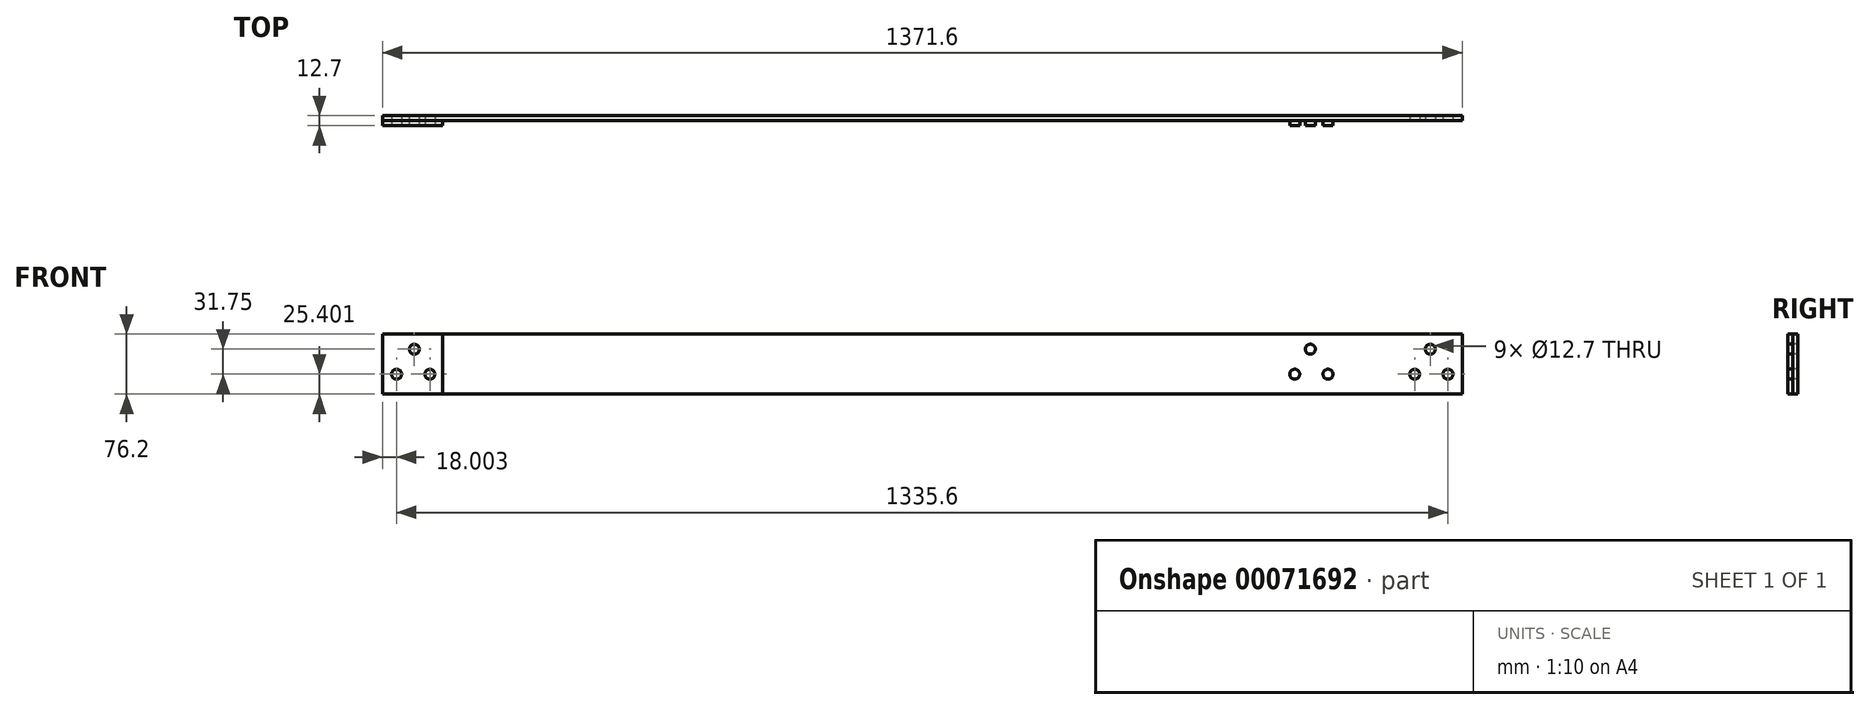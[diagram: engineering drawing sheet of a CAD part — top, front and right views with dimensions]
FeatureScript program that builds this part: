
annotation { "Feature Type Name" : "Feature", "Feature Type Description" : "" }
export const myFeature = defineFeature(function(context is Context, id is Id, definition is map)
    precondition{}
    {
        {
            var Q0;
            Q0=qCreatedBy(makeId("Front.planeOp"),FACE);
            var sketch = newSketch(context, id + "F0", { "sketchPlane" : qUnion([Q0])});
            skLineSegment(sketch, "E0.bottom", {"start": v(-278.67, 72.85) * mm, "end": v(940.53, 72.85) * mm});
            skLineSegment(sketch, "E0.top", {"start": v(-278.67, -3.35) * mm, "end": v(940.53, -3.35) * mm});
            skLineSegment(sketch, "E0.left", {"start": v(-278.67, 72.85) * mm, "end": v(-278.67, -3.35) * mm});
            skLineSegment(sketch, "E0.right", {"start": v(940.53, 72.85) * mm, "end": v(940.53, -3.35) * mm});
            skSolve(sketch);
        }
        {
            var Q0;
            Q0=makeQuery(id+"F0.imprint","IMPRINT",FACE,{"disambiguationData":[TD([[makeQuery(id+"F0.imprint","IMPRINT",EDGE,{"derivedFrom":sQuery(id+"F0.wireOp",EDGE,"E0.bottom")}),-1.0]])]});
            extrude(context, id + "F1", {"entities" : qUnion([Q0]), "depth" : 6.35 * mm});
        }
        {
            var Q0;
            Q0=makeQuery(id+"F1.opExtrude","CAP_FACE",FACE,{"disambiguationData":[OSD([sQuery(id+"F0.wireOp",EDGE,"E0.bottom"),sQuery(id+"F0.wireOp",EDGE,"E0.top"),sQuery(id+"F0.wireOp",EDGE,"E0.left"),sQuery(id+"F0.wireOp",EDGE,"E0.right")])],"isStart":false});
            var sketch = newSketch(context, id + "F2", { "sketchPlane" : qUnion([Q0])});
            skLineSegment(sketch, "E1.0", {"start": v(-278.67, 72.85) * mm, "end": v(940.53, 72.85) * mm});
            skLineSegment(sketch, "E1.1", {"start": v(-278.67, -3.35) * mm, "end": v(940.53, -3.35) * mm});
            skLineSegment(sketch, "E1.2", {"start": v(940.53, 72.85) * mm, "end": v(940.53, -3.35) * mm});
            skLineSegment(sketch, "E1.3", {"start": v(-278.67, 72.85) * mm, "end": v(-278.67, -3.35) * mm});
            skLineSegment(sketch, "E2", {"start": v(-202.47, 72.85) * mm, "end": v(-202.47, -3.35) * mm});
            skCircle(sketch, "E3", {"center": v(-238.17, 53.8) * mm, "radius": 6.35 * mm});
            skCircle(sketch, "E4", {"center": v(-260.67, 22.05) * mm, "radius": 6.35 * mm});
            skCircle(sketch, "E5", {"center": v(-218.33, 22.05) * mm, "radius": 6.35 * mm});
            skLineSegment(sketch, "E6", {"start": v(-278.67, -3.35) * mm, "end": v(-238.17, 53.8) * mm, "construction": true});
            skLineSegment(sketch, "E7", {"start": v(-238.17, 53.8) * mm, "end": v(-202.47, -3.35) * mm, "construction": true});
            skLineSegment(sketch, "E8", {"start": v(330.93, 72.85) * mm, "end": v(330.93, -3.35) * mm, "construction": true});
            skCircle(sketch, "E9.MirrorC", {"center": v(880.2, 22.05) * mm, "radius": 6.35 * mm});
            skCircle(sketch, "E10.MirrorC", {"center": v(900.04, 53.8) * mm, "radius": 6.35 * mm});
            skCircle(sketch, "E11.MirrorC", {"center": v(922.53, 22.05) * mm, "radius": 6.35 * mm});
            skSolve(sketch);
        }
        {
            var Q0;
            Q0=makeQuery(id+"F2.imprint","IMPRINT",FACE,{"disambiguationData":[TD([[makeQuery(id+"F2.imprint","IMPRINT",EDGE,{"derivedFrom":sQuery(id+"F2.wireOp",EDGE,"E3")}),1.0]])]});
            var Q1;
            Q1=makeQuery(id+"F2.imprint","IMPRINT",FACE,{"disambiguationData":[TD([[makeQuery(id+"F2.imprint","IMPRINT",EDGE,{"derivedFrom":sQuery(id+"F2.wireOp",EDGE,"E4")}),1.0]])]});
            var Q2;
            Q2=makeQuery(id+"F2.imprint","IMPRINT",FACE,{"disambiguationData":[TD([[makeQuery(id+"F2.imprint","IMPRINT",EDGE,{"derivedFrom":sQuery(id+"F2.wireOp",EDGE,"E5")}),1.0]])]});
            var Q3;
            Q3=makeQuery(id+"F2.imprint","IMPRINT",FACE,{"disambiguationData":[TD([[makeQuery(id+"F2.imprint","IMPRINT",EDGE,{"derivedFrom":sQuery(id+"F2.wireOp",EDGE,"E10.MirrorC")}),-1.0]])]});
            var Q4;
            Q4=makeQuery(id+"F2.imprint","IMPRINT",FACE,{"disambiguationData":[TD([[makeQuery(id+"F2.imprint","IMPRINT",EDGE,{"derivedFrom":sQuery(id+"F2.wireOp",EDGE,"E9.MirrorC")}),-1.0]])]});
            var Q5;
            Q5=makeQuery(id+"F2.imprint","IMPRINT",FACE,{"disambiguationData":[TD([[makeQuery(id+"F2.imprint","IMPRINT",EDGE,{"derivedFrom":sQuery(id+"F2.wireOp",EDGE,"E11.MirrorC")}),-1.0]])]});
            extrude(context, id + "F3", {"entities" : qUnion([Q0, Q1, Q2, Q3, Q4, Q5]), "operationType" : NewBodyOperationType.REMOVE, "endBound" : BoundingType.THROUGH_ALL, "oppositeDirection" : true, "depth" : 25.4 * mm});
        }
        {
            var Q0;
            Q0=makeQuery(id+"F1.opExtrude","CAP_FACE",FACE,{"disambiguationData":[OSD([sQuery(id+"F0.wireOp",EDGE,"E0.bottom"),sQuery(id+"F0.wireOp",EDGE,"E0.top"),sQuery(id+"F0.wireOp",EDGE,"E0.left"),sQuery(id+"F0.wireOp",EDGE,"E0.right")])],"isStart":true});
            var sketch = newSketch(context, id + "F4", { "sketchPlane" : qUnion([Q0])});
            skCircle(sketch, "E12.0", {"center": v(238.17, 53.8) * mm, "radius": 6.35 * mm});
            skCircle(sketch, "E12.1", {"center": v(218.33, 22.05) * mm, "radius": 6.35 * mm});
            skCircle(sketch, "E12.2", {"center": v(260.67, 22.05) * mm, "radius": 6.35 * mm});
            skLineSegment(sketch, "E12.3", {"start": v(278.67, 72.85) * mm, "end": v(278.67, -3.35) * mm});
            skLineSegment(sketch, "E13", {"start": v(278.67, 72.85) * mm, "end": v(-1092.93, 72.85) * mm});
            skLineSegment(sketch, "E14", {"start": v(278.67, -3.35) * mm, "end": v(-1092.93, -3.35) * mm});
            skLineSegment(sketch, "E15", {"start": v(-1092.93, 72.85) * mm, "end": v(-1092.93, -3.35) * mm});
            skLineSegment(sketch, "E16", {"start": v(-407.13, 72.85) * mm, "end": v(-407.13, -3.35) * mm, "construction": true});
            skCircle(sketch, "E17.MirrorC", {"center": v(-1052.44, 53.8) * mm, "radius": 6.35 * mm});
            skCircle(sketch, "E18.MirrorC", {"center": v(-1074.93, 22.05) * mm, "radius": 6.35 * mm});
            skCircle(sketch, "E19.MirrorC", {"center": v(-1032.6, 22.05) * mm, "radius": 6.35 * mm});
            skSolve(sketch);
        }
        {
            var Q0;
            Q0 = qSketchRegion(id + "F4", true);
            extrude(context, id + "F5", {"entities" : qUnion([Q0]), "depth" : 6.35 * mm});
        }
    });
